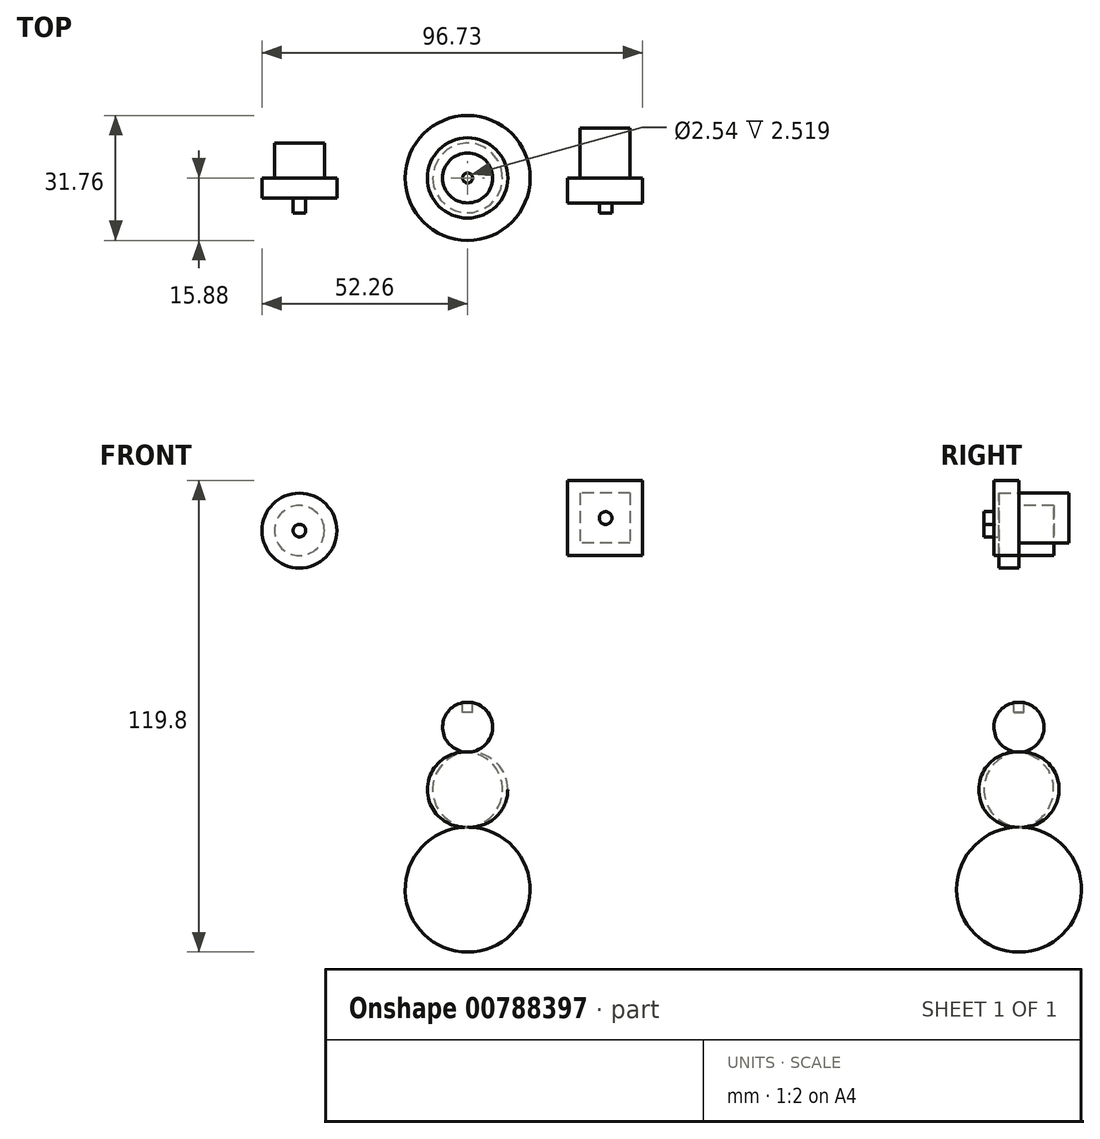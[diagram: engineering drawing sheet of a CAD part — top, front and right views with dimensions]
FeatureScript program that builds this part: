
annotation { "Feature Type Name" : "Feature", "Feature Type Description" : "" }
export const myFeature = defineFeature(function(context is Context, id is Id, definition is map)
    precondition{}
    {
        {
            var Q0;
            Q0=qCreatedBy(makeId("Front.planeOp"),FACE);
            var sketch = newSketch(context, id + "F0", { "sketchPlane" : qUnion([Q0])});
            skLineSegment(sketch, "E0", {"start": v(0, -41.8) * mm, "end": v(0, -73.55) * mm});
            skLineSegment(sketch, "E1", {"start": v(0, -41.8) * mm, "end": v(0, -22.75) * mm});
            skLineSegment(sketch, "E2", {"start": v(0, -22.75) * mm, "end": v(0, -10.05) * mm});
            skArc(sketch, "E3", {"start": v(0, -22.75) * mm, "mid": v(6.35, -16.4) * mm, "end": v(0, -10.05) * mm});
            skArc(sketch, "E4", {"start": v(0, -41.8) * mm, "mid": v(8.89, -32.28) * mm, "end": v(0, -22.75) * mm});
            skArc(sketch, "E5", {"start": v(0, -73.55) * mm, "mid": v(15.88, -57.68) * mm, "end": v(0, -41.8) * mm});
            skSolve(sketch);
        }
        {
            var Q0;
            Q0=makeQuery(id+"F0.imprint","IMPRINT",FACE,{"disambiguationData":[TD([[makeQuery(id+"F0.imprint","IMPRINT",EDGE,{"derivedFrom":sQuery(id+"F0.wireOp",EDGE,"E0")}),1.0]])]});
            var Q1;
            Q1=makeQuery(id+"F0.imprint","IMPRINT",FACE,{"disambiguationData":[TD([[makeQuery(id+"F0.imprint","IMPRINT",EDGE,{"derivedFrom":sQuery(id+"F0.wireOp",EDGE,"E1")}),-1.0]])]});
            var Q2;
            Q2=makeQuery(id+"F0.imprint","IMPRINT",FACE,{"disambiguationData":[TD([[makeQuery(id+"F0.imprint","IMPRINT",EDGE,{"derivedFrom":sQuery(id+"F0.wireOp",EDGE,"E2")}),-1.0]])]});
            var Q3;
            Q3=sQuery(id+"F0.wireOp",EDGE,"E0");
            revolve(context, id + "F1", {"surfaceOperationType" : NewSurfaceOperationType.NEW, "entities" : qUnion([Q0, Q1, Q2]), "axis" : qUnion([Q3]), "revolveType" : RevolveType.FULL});
        }
        {
            var Q0;
            Q0=qCreatedBy(makeId("Top.planeOp"),FACE);
            var sketch = newSketch(context, id + "F2", { "sketchPlane" : qUnion([Q0])});
            skCircle(sketch, "E6", {"center": v(0, 0) * mm, "radius": 1.27 * mm});
            skSolve(sketch);
        }
        {
            var Q0;
            Q0=makeQuery(id+"F2.imprint","IMPRINT",FACE,{"disambiguationData":[TD([[makeQuery(id+"F2.imprint","IMPRINT",EDGE,{"derivedFrom":sQuery(id+"F2.wireOp",EDGE,"E6")}),1.0]])]});
            extrude(context, id + "F3", {"entities" : qUnion([Q0]), "operationType" : NewBodyOperationType.REMOVE, "oppositeDirection" : true, "depth" : 12.7 * mm, "offsetDistance" : 25.4 * mm});
        }
        {
            var Q0;
            Q0=qCreatedBy(makeId("Front.planeOp"),FACE);
            var sketch = newSketch(context, id + "F4", { "sketchPlane" : qUnion([Q0])});
            skCircle(sketch, "E7", {"center": v(-42.74, 33.53) * mm, "radius": 9.53 * mm});
            skSolve(sketch);
        }
        {
            var Q0;
            Q0=makeQuery(id+"F4.imprint","IMPRINT",FACE,{"disambiguationData":[TD([[makeQuery(id+"F4.imprint","IMPRINT",EDGE,{"derivedFrom":sQuery(id+"F4.wireOp",EDGE,"E7")}),1.0]])]});
            extrude(context, id + "F5", {"entities" : qUnion([Q0]), "depth" : 5.08 * mm, "offsetDistance" : 25.4 * mm});
        }
        {
            var Q0;
            Q0=makeQuery(id+"F5.opExtrude","CAP_FACE",FACE,{"disambiguationData":[OSD([sQuery(id+"F4.wireOp",EDGE,"E7")])],"isStart":false});
            var sketch = newSketch(context, id + "F6", { "sketchPlane" : qUnion([Q0])});
            skCircle(sketch, "E8", {"center": v(-42.74, 33.53) * mm, "radius": 1.6 * mm});
            skSolve(sketch);
        }
        {
            var Q0;
            Q0=makeQuery(id+"F6.imprint","IMPRINT",FACE,{"disambiguationData":[TD([[makeQuery(id+"F6.imprint","IMPRINT",EDGE,{"derivedFrom":sQuery(id+"F6.wireOp",EDGE,"E8")}),1.0]])]});
            extrude(context, id + "F7", {"entities" : qUnion([Q0]), "operationType" : NewBodyOperationType.ADD, "depth" : 3.8 * mm, "offsetDistance" : 25.4 * mm});
        }
        {
            var Q0;
            Q0=makeQuery(id+"F5.opExtrude","CAP_FACE",FACE,{"disambiguationData":[OSD([sQuery(id+"F4.wireOp",EDGE,"E7")])],"isStart":true});
            var sketch = newSketch(context, id + "F8", { "sketchPlane" : qUnion([Q0])});
            skCircle(sketch, "E9", {"center": v(42.74, 33.53) * mm, "radius": 6.35 * mm});
            skSolve(sketch);
        }
        {
            var Q0;
            Q0=makeQuery(id+"F8.imprint","IMPRINT",FACE,{"disambiguationData":[TD([[makeQuery(id+"F8.imprint","IMPRINT",EDGE,{"derivedFrom":sQuery(id+"F8.wireOp",EDGE,"E9")}),1.0]])]});
            extrude(context, id + "F9", {"entities" : qUnion([Q0]), "operationType" : NewBodyOperationType.ADD, "depth" : 8.9 * mm, "offsetDistance" : 25.4 * mm});
        }
        {
            var Q0;
            Q0=qCreatedBy(makeId("Front.planeOp"),FACE);
            var sketch = newSketch(context, id + "F10", { "sketchPlane" : qUnion([Q0])});
            skLineSegment(sketch, "E10.bottom", {"start": v(25.42, 46.25) * mm, "end": v(44.47, 46.25) * mm});
            skLineSegment(sketch, "E10.top", {"start": v(25.42, 27.2) * mm, "end": v(44.47, 27.2) * mm});
            skLineSegment(sketch, "E10.left", {"start": v(25.42, 46.25) * mm, "end": v(25.42, 27.2) * mm});
            skLineSegment(sketch, "E10.right", {"start": v(44.47, 46.25) * mm, "end": v(44.47, 27.2) * mm});
            skPoint(sketch, "E10.middle", {"position": v(34.94, 36.72) * mm});
            skSolve(sketch);
        }
        {
            var Q0;
            Q0=makeQuery(id+"F10.imprint","IMPRINT",FACE,{"disambiguationData":[TD([[makeQuery(id+"F10.imprint","IMPRINT",EDGE,{"derivedFrom":sQuery(id+"F10.wireOp",EDGE,"E10.bottom")}),-1.0]])]});
            extrude(context, id + "F11", {"entities" : qUnion([Q0]), "depth" : 6.35 * mm, "offsetDistance" : 25.4 * mm});
        }
        {
            var Q0;
            Q0=makeQuery(id+"F11.opExtrude","CAP_FACE",FACE,{"disambiguationData":[OSD([sQuery(id+"F10.wireOp",EDGE,"E10.bottom"),sQuery(id+"F10.wireOp",EDGE,"E10.top"),sQuery(id+"F10.wireOp",EDGE,"E10.left"),sQuery(id+"F10.wireOp",EDGE,"E10.right")])],"isStart":true});
            var sketch = newSketch(context, id + "F12", { "sketchPlane" : qUnion([Q0])});
            skLineSegment(sketch, "E11.bottom", {"start": v(-41.3, 43.07) * mm, "end": v(-28.6, 43.07) * mm});
            skLineSegment(sketch, "E11.top", {"start": v(-41.3, 30.37) * mm, "end": v(-28.6, 30.37) * mm});
            skLineSegment(sketch, "E11.left", {"start": v(-41.3, 43.07) * mm, "end": v(-41.3, 30.37) * mm});
            skLineSegment(sketch, "E11.right", {"start": v(-28.6, 43.07) * mm, "end": v(-28.6, 30.37) * mm});
            skPoint(sketch, "E11.middle", {"position": v(-34.94, 36.72) * mm});
            skSolve(sketch);
        }
        {
            var Q0;
            Q0=makeQuery(id+"F12.imprint","IMPRINT",FACE,{"disambiguationData":[TD([[makeQuery(id+"F12.imprint","IMPRINT",EDGE,{"derivedFrom":sQuery(id+"F12.wireOp",EDGE,"E11.bottom")}),-1.0]])]});
            extrude(context, id + "F13", {"entities" : qUnion([Q0]), "operationType" : NewBodyOperationType.ADD, "depth" : 12.7 * mm, "offsetDistance" : 25.4 * mm});
        }
        {
            var Q0;
            Q0=makeQuery(id+"F11.opExtrude","CAP_FACE",FACE,{"disambiguationData":[OSD([sQuery(id+"F10.wireOp",EDGE,"E10.bottom"),sQuery(id+"F10.wireOp",EDGE,"E10.top"),sQuery(id+"F10.wireOp",EDGE,"E10.left"),sQuery(id+"F10.wireOp",EDGE,"E10.right")])],"isStart":false});
            var sketch = newSketch(context, id + "F14", { "sketchPlane" : qUnion([Q0])});
            skCircle(sketch, "E12", {"center": v(35.06, 36.72) * mm, "radius": 1.61 * mm});
            skPoint(sketch, "E12.centerSnap0", {"position": v(25.42, 36.72) * mm});
            skSolve(sketch);
        }
        {
            var Q0;
            Q0=makeQuery(id+"F14.imprint","IMPRINT",FACE,{"disambiguationData":[TD([[makeQuery(id+"F14.imprint","IMPRINT",EDGE,{"derivedFrom":sQuery(id+"F14.wireOp",EDGE,"E12")}),1.0]])]});
            extrude(context, id + "F15", {"entities" : qUnion([Q0]), "operationType" : NewBodyOperationType.ADD, "depth" : 2.54 * mm, "offsetDistance" : 25.4 * mm});
        }
    });
